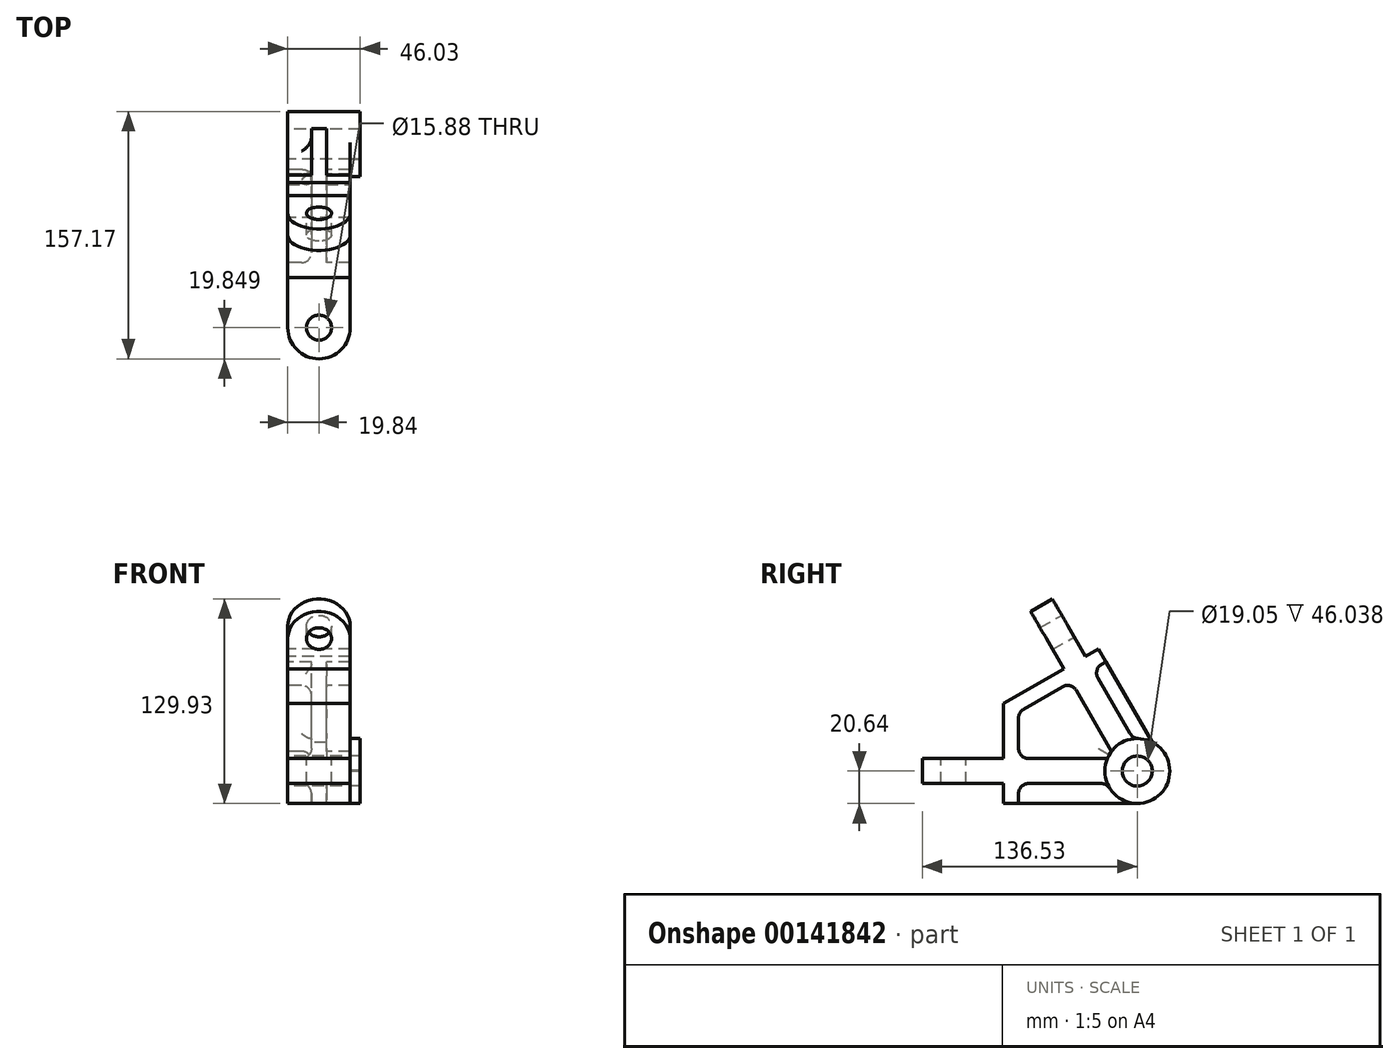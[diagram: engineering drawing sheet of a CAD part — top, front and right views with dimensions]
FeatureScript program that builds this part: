
annotation { "Feature Type Name" : "Feature", "Feature Type Description" : "" }
export const myFeature = defineFeature(function(context is Context, id is Id, definition is map)
    precondition{}
    {
        {
            var Q0;
            Q0=qCreatedBy(makeId("Right.planeOp"),FACE);
            var sketch = newSketch(context, id + "F0", { "sketchPlane" : qUnion([Q0])});
            skArc(sketch, "E0", {"start": v(-16.4, 12.53) * mm, "mid": v(-17.87, 10.32) * mm, "end": v(-19.05, 7.94) * mm});
            skCircle(sketch, "E1", {"center": v(0, 0) * mm, "radius": 9.53 * mm});
            skLineSegment(sketch, "E2.0", {"start": v(-2.65, 20.47) * mm, "end": v(-28.16, 64.64) * mm});
            skLineSegment(sketch, "E3.0", {"start": v(-9.17, 0) * mm, "end": v(-9.5, 0.6) * mm});
            skLineSegment(sketch, "E4", {"start": v(-53.93, 109.29) * mm, "end": v(-67.68, 101.35) * mm});
            skLineSegment(sketch, "E5", {"start": v(0, 0) * mm, "end": v(-9.52, 0) * mm});
            skLineSegment(sketch, "E6", {"start": v(-136.53, -7.94) * mm, "end": v(-136.53, 7.94) * mm});
            skLineSegment(sketch, "E7.trimOffspring", {"start": v(-16.4, 12.53) * mm, "end": v(-41.9, 56.7) * mm});
            skLineSegment(sketch, "E8.trimOffspring", {"start": v(-19.05, 7.94) * mm, "end": v(-75.4, 7.94) * mm});
            skLineSegment(sketch, "E9.trimOffspring", {"start": v(-19.05, -7.94) * mm, "end": v(-75.4, -7.94) * mm});
            skLineSegment(sketch, "E10.0", {"start": v(-84.93, -20.64) * mm, "end": v(-84.93, -7.94) * mm});
            skLineSegment(sketch, "E11", {"start": v(-84.93, 7.94) * mm, "end": v(-84.93, 42.86) * mm});
            skLineSegment(sketch, "E12", {"start": v(-84.93, 42.86) * mm, "end": v(-46.67, 64.95) * mm});
            skLineSegment(sketch, "E13.0", {"start": v(-19.9, 69.4) * mm, "end": v(-24.67, 77.65) * mm});
            skLineSegment(sketch, "E14.0", {"start": v(-28.16, 64.64) * mm, "end": v(-19.9, 69.4) * mm});
            skLineSegment(sketch, "E15.0", {"start": v(-75.4, 37.36) * mm, "end": v(-41.9, 56.7) * mm});
            skLineSegment(sketch, "E16.0", {"start": v(-75.4, -20.64) * mm, "end": v(-75.4, -7.94) * mm});
            skLineSegment(sketch, "E17.trimOffspring", {"start": v(-32.92, 72.9) * mm, "end": v(-24.67, 77.65) * mm});
            skLineSegment(sketch, "E18.trimOffspring", {"start": v(-32.92, 72.9) * mm, "end": v(-53.93, 109.29) * mm});
            skLineSegment(sketch, "E19.trimOffspring", {"start": v(-46.67, 64.95) * mm, "end": v(-67.68, 101.35) * mm});
            skLineSegment(sketch, "E20.0", {"start": v(-75.4, -20.64) * mm, "end": v(-84.93, -20.64) * mm});
            skLineSegment(sketch, "E21.trimOffspring", {"start": v(-84.93, -7.94) * mm, "end": v(-136.53, -7.94) * mm});
            skLineSegment(sketch, "E22.trimOffspring", {"start": v(-84.93, 7.94) * mm, "end": v(-136.53, 7.94) * mm});
            skLineSegment(sketch, "E23.trimOffspring", {"start": v(-75.4, 7.94) * mm, "end": v(-75.4, 37.36) * mm});
            skArc(sketch, "E24.trimOffspring", {"start": v(-19.05, -7.94) * mm, "mid": v(17.87, -10.32) * mm, "end": v(-2.65, 20.47) * mm});
            skLineSegment(sketch, "E25.0", {"start": v(9.62, 18.26) * mm, "end": v(-19.9, 69.4) * mm});
            skLineSegment(sketch, "E26", {"start": v(-75.4, -20.64) * mm, "end": v(0, -20.64) * mm});
            skSolve(sketch);
        }
        {
            var Q0;
            Q0=makeQuery(id+"F0.imprint","IMPRINT",FACE,{"disambiguationData":[TD([[makeQuery(id+"F0.imprint","IMPRINT",EDGE,{"derivedFrom":sQuery(id+"F0.wireOp",EDGE,"E0")}),1.0]])]});
            extrude(context, id + "F1", {"entities" : qUnion([Q0]), "endBound" : BoundingType.SYMMETRIC, "depth" : 39.69 * mm});
        }
        {
            var Q0;
            Q0=makeQuery(id+"F0.imprint","IMPRINT",FACE,{"disambiguationData":[TD([[makeQuery(id+"F0.imprint","IMPRINT",EDGE,{"derivedFrom":sQuery(id+"F0.wireOp",EDGE,"E0")}),-1.0]])]});
            var Q1;
            {var subQ0=sQuery(id+"F0.wireOp",EDGE,"E2.0");Q1=makeQuery(id+"F0.imprint","IMPRINT",FACE,{"disambiguationData":[TD([[makeQuery(id+"F0.imprint","IMPRINT",EDGE,{"derivedFrom":subQ0}),-1.0]])]});}
            var Q2;
            {var subQ0=sQuery(id+"F0.wireOp",EDGE,"E9.trimOffspring");Q2=makeQuery(id+"F0.imprint","IMPRINT",FACE,{"disambiguationData":[TD([[makeQuery(id+"F0.imprint","IMPRINT",EDGE,{"derivedFrom":subQ0}),1.0]])]});}
            extrude(context, id + "F2", {"entities" : qUnion([Q0, Q1, Q2]), "operationType" : NewBodyOperationType.ADD, "endBound" : BoundingType.SYMMETRIC, "depth" : 9.52 * mm});
        }
        {
            var Q0;
            Q0=makeQuery(id+"F1.opExtrude","CAP_EDGE",EDGE,{"disambiguationData":[OSD([sQuery(id+"F0.wireOp",EDGE,"E4")])],"isStart":false});
            var Q1;
            Q1=makeQuery(id+"F1.opExtrude","CAP_EDGE",EDGE,{"disambiguationData":[OSD([sQuery(id+"F0.wireOp",EDGE,"E4")])],"isStart":true});
            var Q2;
            Q2=makeQuery(id+"F1.opExtrude","CAP_EDGE",EDGE,{"disambiguationData":[OSD([sQuery(id+"F0.wireOp",EDGE,"E6")])],"isStart":false});
            var Q3;
            Q3=makeQuery(id+"F1.opExtrude","CAP_EDGE",EDGE,{"disambiguationData":[OSD([sQuery(id+"F0.wireOp",EDGE,"E6")])],"isStart":true});
            fillet(context, id + "F3", {"entities" : qUnion([Q0, Q1, Q2, Q3]), "radius" : 19.84 * mm, "tangentPropagation" : true, "allowEdgeOverflow" : false});
        }
        {
            var Q0;
            Q0=makeQuery(id+"F1.opExtrude","SWEPT_FACE",FACE,{"disambiguationData":[OSD([sQuery(id+"F0.wireOp",EDGE,"E22.trimOffspring")])]});
            var sketch = newSketch(context, id + "F4", { "sketchPlane" : qUnion([Q0])});
            skCircle(sketch, "E27", {"center": v(0, -116.68) * mm, "radius": 7.94 * mm});
            skSolve(sketch);
        }
        {
            var Q0;
            Q0=makeQuery(id+"F4.imprint","IMPRINT",FACE,{"disambiguationData":[TD([[makeQuery(id+"F4.imprint","IMPRINT",EDGE,{"derivedFrom":sQuery(id+"F4.wireOp",EDGE,"E27")}),1.0]])]});
            extrude(context, id + "F5", {"entities" : qUnion([Q0]), "operationType" : NewBodyOperationType.REMOVE, "oppositeDirection" : true, "depth" : 25.4 * mm});
        }
        {
            var Q0;
            Q0=makeQuery(id+"F1.opExtrude","SWEPT_FACE",FACE,{"disambiguationData":[OSD([sQuery(id+"F0.wireOp",EDGE,"E18.trimOffspring")])]});
            var sketch = newSketch(context, id + "F6", { "sketchPlane" : qUnion([Q0])});
            skCircle(sketch, "E28", {"center": v(0, 101.77) * mm, "radius": 7.94 * mm});
            skSolve(sketch);
        }
        {
            var Q0;
            Q0 = qSketchRegion(id + "F6", true);
            extrude(context, id + "F7", {"entities" : qUnion([Q0]), "operationType" : NewBodyOperationType.REMOVE, "oppositeDirection" : true, "depth" : 25.4 * mm});
        }
        {
            var Q0;
            Q0=makeQuery(id+"F1.opExtrude","CAP_FACE",FACE,{"disambiguationData":[OSD([sQuery(id+"F0.wireOp",EDGE,"E0"),sQuery(id+"F0.wireOp",EDGE,"E1"),sQuery(id+"F0.wireOp",EDGE,"E2.0"),sQuery(id+"F0.wireOp",EDGE,"E4"),sQuery(id+"F0.wireOp",EDGE,"E6"),sQuery(id+"F0.wireOp",EDGE,"E7.trimOffspring"),sQuery(id+"F0.wireOp",EDGE,"E8.trimOffspring"),sQuery(id+"F0.wireOp",EDGE,"E9.trimOffspring"),sQuery(id+"F0.wireOp",EDGE,"E10.0"),sQuery(id+"F0.wireOp",EDGE,"E11"),sQuery(id+"F0.wireOp",EDGE,"E12"),sQuery(id+"F0.wireOp",EDGE,"E13.0"),sQuery(id+"F0.wireOp",EDGE,"E15.0"),sQuery(id+"F0.wireOp",EDGE,"E16.0"),sQuery(id+"F0.wireOp",EDGE,"E17.trimOffspring"),sQuery(id+"F0.wireOp",EDGE,"E14.0"),sQuery(id+"F0.wireOp",EDGE,"E18.trimOffspring"),sQuery(id+"F0.wireOp",EDGE,"E19.trimOffspring"),sQuery(id+"F0.wireOp",EDGE,"E20.0"),sQuery(id+"F0.wireOp",EDGE,"E21.trimOffspring"),sQuery(id+"F0.wireOp",EDGE,"E22.trimOffspring"),sQuery(id+"F0.wireOp",EDGE,"E23.trimOffspring"),sQuery(id+"F0.wireOp",EDGE,"E24.trimOffspring")])],"isStart":false});
            var sketch = newSketch(context, id + "F8", { "sketchPlane" : qUnion([Q0])});
            skCircle(sketch, "E29", {"center": v(0, 0) * mm, "radius": 20.64 * mm});
            skSolve(sketch);
        }
        {
            var Q0;
            Q0 = qSketchRegion(id + "F8", true);
            extrude(context, id + "F9", {"entities" : qUnion([Q0]), "operationType" : NewBodyOperationType.ADD, "depth" : 6.35 * mm});
        }
        {
            var Q0;
            {var subQ0=sQuery(id+"F0.wireOp",EDGE,"E3.0");Q0=makeQuery(id+"F0.imprint","IMPRINT",FACE,{"disambiguationData":[TD([[makeQuery(id+"F0.imprint","IMPRINT",EDGE,{"derivedFrom":subQ0}),-1.0]])]});}
            extrude(context, id + "F10", {"entities" : qUnion([Q0]), "operationType" : NewBodyOperationType.REMOVE, "endBound" : BoundingType.SYMMETRIC, "oppositeDirection" : true, "depth" : 76.2 * mm});
        }
        {
            var Q0;
            {var subQ0=sQuery(id+"F0.wireOp",EDGE,"E23.trimOffspring");var subQ1=sQuery(id+"F0.wireOp",EDGE,"E15.0");var subQ2=sQuery(id+"F0.wireOp",EDGE,"E8.trimOffspring");var subQ3=sQuery(id+"F0.wireOp",EDGE,"E7.trimOffspring");var subQ4=sQuery(id+"F0.wireOp",EDGE,"E0");Q0=makeQuery(id+"F2.boolean.opBoolean","SPLIT",EDGE,{"disambiguationData":[TD([makeQuery(id+"F2.opExtrude","CAP_FACE",FACE,{"disambiguationData":[OSD([subQ4,subQ3,subQ2,subQ1,subQ0])],"isStart":false})])],"derivedFrom":makeQuery(id+"F1.opExtrude","SWEPT_EDGE",EDGE,{"disambiguationData":[OSD([subQ3,subQ1])]})});}
            var Q1;
            {var subQ0=sQuery(id+"F0.wireOp",EDGE,"E23.trimOffspring");var subQ1=sQuery(id+"F0.wireOp",EDGE,"E15.0");var subQ2=sQuery(id+"F0.wireOp",EDGE,"E8.trimOffspring");var subQ3=sQuery(id+"F0.wireOp",EDGE,"E7.trimOffspring");var subQ4=sQuery(id+"F0.wireOp",EDGE,"E0");Q1=makeQuery(id+"F2.boolean.opBoolean","SPLIT",EDGE,{"disambiguationData":[TD([makeQuery(id+"F2.opExtrude","CAP_FACE",FACE,{"disambiguationData":[OSD([subQ4,subQ3,subQ2,subQ1,subQ0])],"isStart":false})])],"derivedFrom":makeQuery(id+"F1.opExtrude","SWEPT_EDGE",EDGE,{"disambiguationData":[OSD([subQ1,subQ0])]})});}
            var Q2;
            {var subQ0=sQuery(id+"F0.wireOp",EDGE,"E23.trimOffspring");var subQ1=sQuery(id+"F0.wireOp",EDGE,"E15.0");var subQ2=sQuery(id+"F0.wireOp",EDGE,"E8.trimOffspring");var subQ3=sQuery(id+"F0.wireOp",EDGE,"E7.trimOffspring");var subQ4=sQuery(id+"F0.wireOp",EDGE,"E0");Q2=makeQuery(id+"F2.boolean.opBoolean","SPLIT",EDGE,{"disambiguationData":[TD([makeQuery(id+"F2.opExtrude","CAP_FACE",FACE,{"disambiguationData":[OSD([subQ4,subQ3,subQ2,subQ1,subQ0])],"isStart":false})])],"derivedFrom":makeQuery(id+"F1.opExtrude","SWEPT_EDGE",EDGE,{"disambiguationData":[OSD([subQ2,subQ0])]})});}
            var Q3;
            {var subQ0=sQuery(id+"F0.wireOp",EDGE,"E24.trimOffspring");var subQ1=sQuery(id+"F0.wireOp",EDGE,"E14.0");var subQ2=sQuery(id+"F0.wireOp",EDGE,"E2.0");Q3=makeQuery(id+"F2.boolean.opBoolean","SPLIT",EDGE,{"disambiguationData":[TD([makeQuery(id+"F2.opExtrude","CAP_FACE",FACE,{"disambiguationData":[OSD([subQ2,subQ1,subQ0,sQuery(id+"F0.wireOp",EDGE,"E25.0")])],"isStart":false})])],"derivedFrom":makeQuery(id+"F1.opExtrude","SWEPT_EDGE",EDGE,{"disambiguationData":[OSD([subQ2,subQ1])]})});}
            var Q4;
            {var subQ0=sQuery(id+"F0.wireOp",EDGE,"E24.trimOffspring");var subQ1=sQuery(id+"F0.wireOp",EDGE,"E14.0");var subQ2=sQuery(id+"F0.wireOp",EDGE,"E2.0");Q4=makeQuery(id+"F2.boolean.opBoolean","SPLIT",EDGE,{"disambiguationData":[TD([makeQuery(id+"F2.opExtrude","CAP_FACE",FACE,{"disambiguationData":[OSD([subQ2,subQ1,subQ0,sQuery(id+"F0.wireOp",EDGE,"E25.0")])],"isStart":false})])],"derivedFrom":makeQuery(id+"F1.opExtrude","SWEPT_EDGE",EDGE,{"disambiguationData":[OSD([subQ2,subQ0])]})});}
            var Q5;
            {var subQ0=sQuery(id+"F0.wireOp",EDGE,"E24.trimOffspring");var subQ1=sQuery(id+"F0.wireOp",EDGE,"E14.0");var subQ2=sQuery(id+"F0.wireOp",EDGE,"E2.0");Q5=makeQuery(id+"F2.boolean.opBoolean","SPLIT",EDGE,{"disambiguationData":[TD([makeQuery(id+"F2.opExtrude","CAP_FACE",FACE,{"disambiguationData":[OSD([subQ2,subQ1,subQ0,sQuery(id+"F0.wireOp",EDGE,"E25.0")])],"isStart":true})])],"derivedFrom":makeQuery(id+"F1.opExtrude","SWEPT_EDGE",EDGE,{"disambiguationData":[OSD([subQ2,subQ0])]})});}
            var Q6;
            {var subQ0=sQuery(id+"F0.wireOp",EDGE,"E24.trimOffspring");var subQ1=sQuery(id+"F0.wireOp",EDGE,"E14.0");var subQ2=sQuery(id+"F0.wireOp",EDGE,"E2.0");Q6=makeQuery(id+"F2.boolean.opBoolean","SPLIT",EDGE,{"disambiguationData":[TD([makeQuery(id+"F2.opExtrude","CAP_FACE",FACE,{"disambiguationData":[OSD([subQ2,subQ1,subQ0,sQuery(id+"F0.wireOp",EDGE,"E25.0")])],"isStart":true})])],"derivedFrom":makeQuery(id+"F1.opExtrude","SWEPT_EDGE",EDGE,{"disambiguationData":[OSD([subQ2,subQ1])]})});}
            var Q7;
            {var subQ0=sQuery(id+"F0.wireOp",EDGE,"E23.trimOffspring");var subQ1=sQuery(id+"F0.wireOp",EDGE,"E15.0");var subQ2=sQuery(id+"F0.wireOp",EDGE,"E8.trimOffspring");var subQ3=sQuery(id+"F0.wireOp",EDGE,"E7.trimOffspring");var subQ4=sQuery(id+"F0.wireOp",EDGE,"E0");Q7=makeQuery(id+"F2.boolean.opBoolean","SPLIT",EDGE,{"disambiguationData":[TD([makeQuery(id+"F2.opExtrude","CAP_FACE",FACE,{"disambiguationData":[OSD([subQ4,subQ3,subQ2,subQ1,subQ0])],"isStart":true})])],"derivedFrom":makeQuery(id+"F1.opExtrude","SWEPT_EDGE",EDGE,{"disambiguationData":[OSD([subQ1,subQ0])]})});}
            var Q8;
            {var subQ0=sQuery(id+"F0.wireOp",EDGE,"E23.trimOffspring");var subQ1=sQuery(id+"F0.wireOp",EDGE,"E15.0");var subQ2=sQuery(id+"F0.wireOp",EDGE,"E8.trimOffspring");var subQ3=sQuery(id+"F0.wireOp",EDGE,"E7.trimOffspring");var subQ4=sQuery(id+"F0.wireOp",EDGE,"E0");Q8=makeQuery(id+"F2.boolean.opBoolean","SPLIT",EDGE,{"disambiguationData":[TD([makeQuery(id+"F2.opExtrude","CAP_FACE",FACE,{"disambiguationData":[OSD([subQ4,subQ3,subQ2,subQ1,subQ0])],"isStart":true})])],"derivedFrom":makeQuery(id+"F1.opExtrude","SWEPT_EDGE",EDGE,{"disambiguationData":[OSD([subQ3,subQ1])]})});}
            var Q9;
            {var subQ0=sQuery(id+"F0.wireOp",EDGE,"E23.trimOffspring");var subQ1=sQuery(id+"F0.wireOp",EDGE,"E15.0");var subQ2=sQuery(id+"F0.wireOp",EDGE,"E8.trimOffspring");var subQ3=sQuery(id+"F0.wireOp",EDGE,"E7.trimOffspring");var subQ4=sQuery(id+"F0.wireOp",EDGE,"E0");Q9=makeQuery(id+"F2.boolean.opBoolean","SPLIT",EDGE,{"disambiguationData":[TD([makeQuery(id+"F2.opExtrude","CAP_FACE",FACE,{"disambiguationData":[OSD([subQ4,subQ3,subQ2,subQ1,subQ0])],"isStart":true})])],"derivedFrom":makeQuery(id+"F1.opExtrude","SWEPT_EDGE",EDGE,{"disambiguationData":[OSD([subQ2,subQ0])]})});}
            var Q10;
            {var subQ0=sQuery(id+"F0.wireOp",EDGE,"E24.trimOffspring");var subQ1=sQuery(id+"F0.wireOp",EDGE,"E16.0");var subQ2=sQuery(id+"F0.wireOp",EDGE,"E9.trimOffspring");Q10=makeQuery(id+"F2.boolean.opBoolean","SPLIT",EDGE,{"disambiguationData":[TD([makeQuery(id+"F2.opExtrude","CAP_FACE",FACE,{"disambiguationData":[OSD([subQ2,subQ1,subQ0,sQuery(id+"F0.wireOp",EDGE,"E26")])],"isStart":true})])],"derivedFrom":makeQuery(id+"F1.opExtrude","SWEPT_EDGE",EDGE,{"disambiguationData":[OSD([subQ2,subQ1])]})});}
            var Q11;
            {var subQ0=sQuery(id+"F0.wireOp",EDGE,"E24.trimOffspring");var subQ1=sQuery(id+"F0.wireOp",EDGE,"E16.0");var subQ2=sQuery(id+"F0.wireOp",EDGE,"E9.trimOffspring");Q11=makeQuery(id+"F2.boolean.opBoolean","SPLIT",EDGE,{"disambiguationData":[TD([makeQuery(id+"F2.opExtrude","CAP_FACE",FACE,{"disambiguationData":[OSD([subQ2,subQ1,subQ0,sQuery(id+"F0.wireOp",EDGE,"E26")])],"isStart":true})])],"derivedFrom":makeQuery(id+"F1.opExtrude","SWEPT_EDGE",EDGE,{"disambiguationData":[OSD([subQ2,subQ0])]})});}
            var Q12;
            Q12=makeQuery(id+"F2.opExtrude","CAP_EDGE",EDGE,{"disambiguationData":[OSD([sQuery(id+"F0.wireOp",EDGE,"E9.trimOffspring")])],"isStart":true});
            var Q13;
            Q13=makeQuery(id+"F2.opExtrude","CAP_EDGE",EDGE,{"disambiguationData":[OSD([sQuery(id+"F0.wireOp",EDGE,"E8.trimOffspring")])],"isStart":true});
            var Q14;
            Q14=makeQuery(id+"F2.opExtrude","CAP_EDGE",EDGE,{"disambiguationData":[OSD([sQuery(id+"F0.wireOp",EDGE,"E23.trimOffspring")])],"isStart":true});
            var Q15;
            Q15=makeQuery(id+"F2.opExtrude","CAP_EDGE",EDGE,{"disambiguationData":[OSD([sQuery(id+"F0.wireOp",EDGE,"E15.0")])],"isStart":true});
            var Q16;
            Q16=makeQuery(id+"F2.opExtrude","CAP_EDGE",EDGE,{"disambiguationData":[OSD([sQuery(id+"F0.wireOp",EDGE,"E7.trimOffspring")])],"isStart":true});
            var Q17;
            Q17=makeQuery(id+"F2.opExtrude","CAP_EDGE",EDGE,{"disambiguationData":[OSD([sQuery(id+"F0.wireOp",EDGE,"E0")])],"isStart":true});
            var Q18;
            Q18=makeQuery(id+"F2.opExtrude","CAP_EDGE",EDGE,{"disambiguationData":[OSD([sQuery(id+"F0.wireOp",EDGE,"E9.trimOffspring")])],"isStart":false});
            var Q19;
            {var subQ0=sQuery(id+"F0.wireOp",EDGE,"E24.trimOffspring");var subQ1=sQuery(id+"F0.wireOp",EDGE,"E16.0");var subQ2=sQuery(id+"F0.wireOp",EDGE,"E9.trimOffspring");Q19=makeQuery(id+"F2.boolean.opBoolean","SPLIT",EDGE,{"disambiguationData":[TD([makeQuery(id+"F2.opExtrude","CAP_FACE",FACE,{"disambiguationData":[OSD([subQ2,subQ1,subQ0,sQuery(id+"F0.wireOp",EDGE,"E26")])],"isStart":false})])],"derivedFrom":makeQuery(id+"F1.opExtrude","SWEPT_EDGE",EDGE,{"disambiguationData":[OSD([subQ2,subQ0])]})});}
            var Q20;
            Q20=makeQuery(id+"F2.opExtrude","CAP_EDGE",EDGE,{"disambiguationData":[OSD([sQuery(id+"F0.wireOp",EDGE,"E16.0")])],"isStart":false});
            var Q21;
            {var subQ0=sQuery(id+"F0.wireOp",EDGE,"E24.trimOffspring");var subQ1=sQuery(id+"F0.wireOp",EDGE,"E16.0");var subQ2=sQuery(id+"F0.wireOp",EDGE,"E9.trimOffspring");Q21=makeQuery(id+"F2.boolean.opBoolean","SPLIT",EDGE,{"disambiguationData":[TD([makeQuery(id+"F2.opExtrude","CAP_FACE",FACE,{"disambiguationData":[OSD([subQ2,subQ1,subQ0,sQuery(id+"F0.wireOp",EDGE,"E26")])],"isStart":false})])],"derivedFrom":makeQuery(id+"F1.opExtrude","SWEPT_EDGE",EDGE,{"disambiguationData":[OSD([subQ2,subQ1])]})});}
            var Q22;
            Q22=makeQuery(id+"F2.opExtrude","CAP_EDGE",EDGE,{"disambiguationData":[OSD([sQuery(id+"F0.wireOp",EDGE,"E16.0")])],"isStart":true});
            var Q23;
            Q23=makeQuery(id+"F2.opExtrude","CAP_EDGE",EDGE,{"disambiguationData":[OSD([sQuery(id+"F0.wireOp",EDGE,"E2.0")])],"isStart":false});
            var Q24;
            Q24=makeQuery(id+"F2.opExtrude","CAP_EDGE",EDGE,{"disambiguationData":[OSD([sQuery(id+"F0.wireOp",EDGE,"E14.0")])],"isStart":false});
            var Q25;
            {var subQ0=sQuery(id+"F0.wireOp",EDGE,"E24.trimOffspring");Q25=makeQuery(id+"F2.opExtrude","CAP_EDGE",EDGE,{"disambiguationData":[OSD([subQ0]),TDD([makeQuery(id+"F0.imprint","IMPRINT",EDGE,{"disambiguationData":[TD([[makeQuery(id+"F0.imprint","INTERSECT",VERTEX,{"derivedFrom":[sQuery(id+"F0.wireOp",EDGE,"E2.0"),subQ0]}),1.0]])],"derivedFrom":subQ0})])],"isStart":false});}
            var Q26;
            Q26=makeQuery(id+"F2.opExtrude","CAP_EDGE",EDGE,{"disambiguationData":[OSD([sQuery(id+"F0.wireOp",EDGE,"E14.0")])],"isStart":true});
            var Q27;
            Q27=makeQuery(id+"F2.opExtrude","CAP_EDGE",EDGE,{"disambiguationData":[OSD([sQuery(id+"F0.wireOp",EDGE,"E2.0")])],"isStart":true});
            var Q28;
            {var subQ0=sQuery(id+"F0.wireOp",EDGE,"E24.trimOffspring");Q28=makeQuery(id+"F2.opExtrude","CAP_EDGE",EDGE,{"disambiguationData":[OSD([subQ0]),TDD([makeQuery(id+"F0.imprint","IMPRINT",EDGE,{"disambiguationData":[TD([[makeQuery(id+"F0.imprint","INTERSECT",VERTEX,{"derivedFrom":[sQuery(id+"F0.wireOp",EDGE,"E2.0"),subQ0]}),1.0]])],"derivedFrom":subQ0})])],"isStart":true});}
            var Q29;
            Q29=makeQuery(id+"F2.opExtrude","CAP_EDGE",EDGE,{"disambiguationData":[OSD([sQuery(id+"F0.wireOp",EDGE,"E15.0")])],"isStart":false});
            var Q30;
            Q30=makeQuery(id+"F2.opExtrude","CAP_EDGE",EDGE,{"disambiguationData":[OSD([sQuery(id+"F0.wireOp",EDGE,"E23.trimOffspring")])],"isStart":false});
            var Q31;
            Q31=makeQuery(id+"F2.opExtrude","CAP_EDGE",EDGE,{"disambiguationData":[OSD([sQuery(id+"F0.wireOp",EDGE,"E8.trimOffspring")])],"isStart":false});
            var Q32;
            Q32=makeQuery(id+"F2.opExtrude","CAP_EDGE",EDGE,{"disambiguationData":[OSD([sQuery(id+"F0.wireOp",EDGE,"E7.trimOffspring")])],"isStart":false});
            fillet(context, id + "F11", {"entities" : qUnion([Q0, Q1, Q2, Q3, Q4, Q5, Q6, Q7, Q8, Q9, Q10, Q11, Q12, Q13, Q14, Q15, Q16, Q17, Q18, Q19, Q20, Q21, Q22, Q23, Q24, Q25, Q26, Q27, Q28, Q29, Q30, Q31, Q32]), "radius" : 6.35 * mm, "tangentPropagation" : true, "allowEdgeOverflow" : false});
        }
    });
